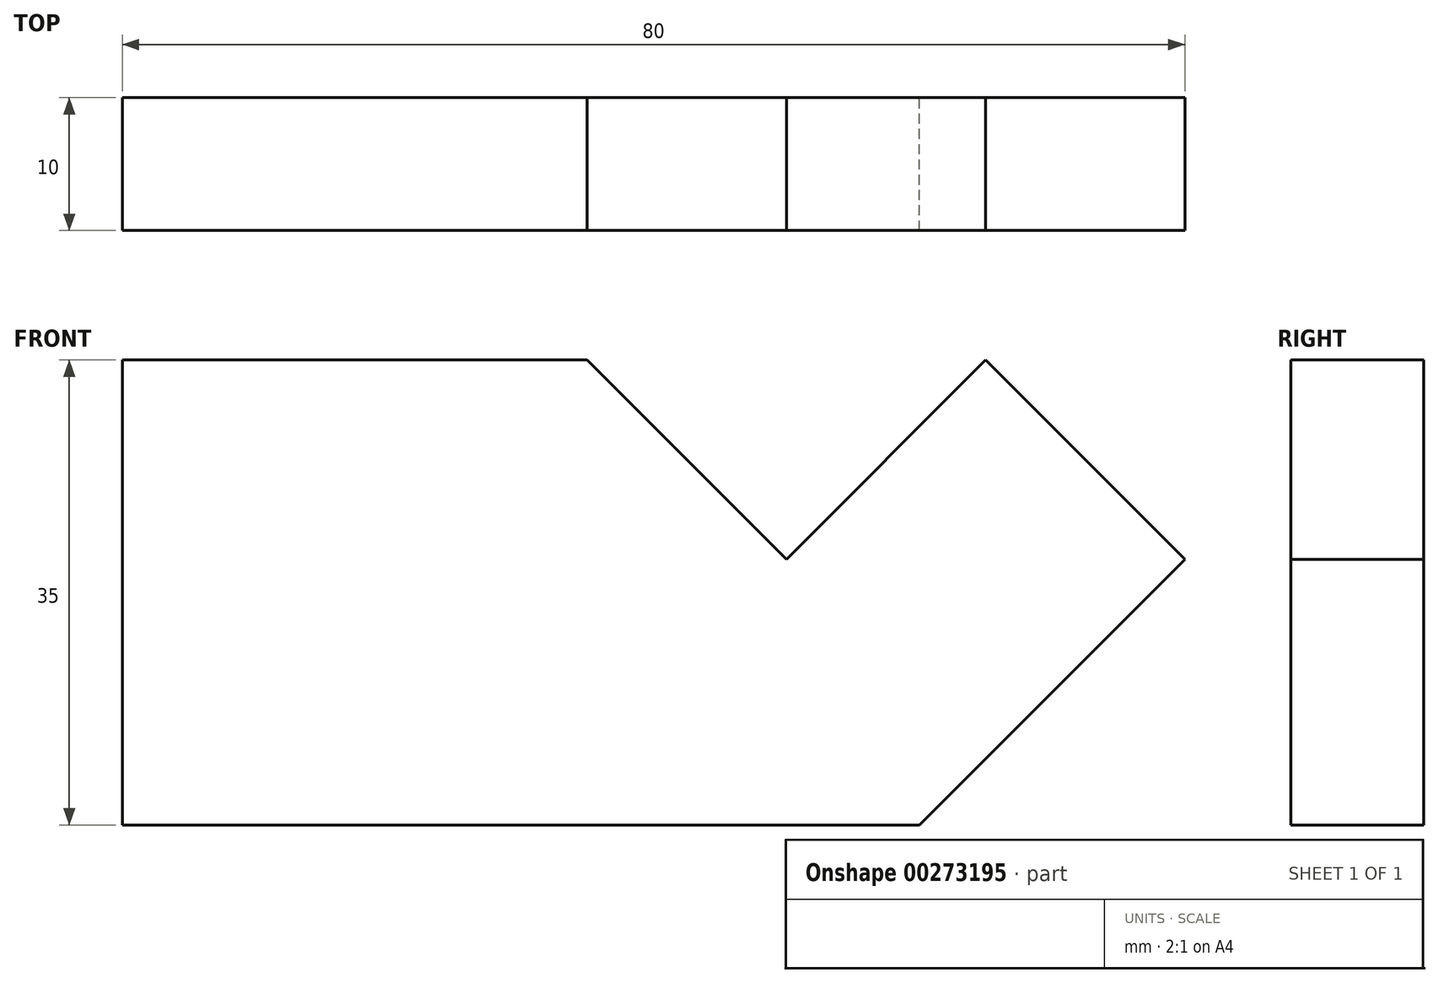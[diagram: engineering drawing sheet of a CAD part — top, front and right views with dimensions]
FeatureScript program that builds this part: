
annotation { "Feature Type Name" : "Feature", "Feature Type Description" : "" }
export const myFeature = defineFeature(function(context is Context, id is Id, definition is map)
    precondition{}
    {
        {
            var Q0;
            Q0=qCreatedBy(makeId("Front.planeOp"),FACE);
            var sketch = newSketch(context, id + "F0", { "sketchPlane" : qUnion([Q0])});
            skLineSegment(sketch, "E0", {"start": v(0, 0) * mm, "end": v(0, 35) * mm});
            skLineSegment(sketch, "E1", {"start": v(0, 35) * mm, "end": v(35, 35) * mm});
            skLineSegment(sketch, "E2", {"start": v(35, 35) * mm, "end": v(50, 20) * mm});
            skLineSegment(sketch, "E3", {"start": v(50, 20) * mm, "end": v(65, 35) * mm});
            skLineSegment(sketch, "E4", {"start": v(60, 0) * mm, "end": v(0, 0) * mm});
            skLineSegment(sketch, "E5", {"start": v(65, 35) * mm, "end": v(80, 20) * mm});
            skLineSegment(sketch, "E6", {"start": v(80, 20) * mm, "end": v(60, 0) * mm});
            skSolve(sketch);
        }
        {
            var Q0;
            Q0 = qSketchRegion(id + "F0", true);
            extrude(context, id + "F1", {"entities" : qUnion([Q0]), "depth" : 10 * mm});
        }
    });
